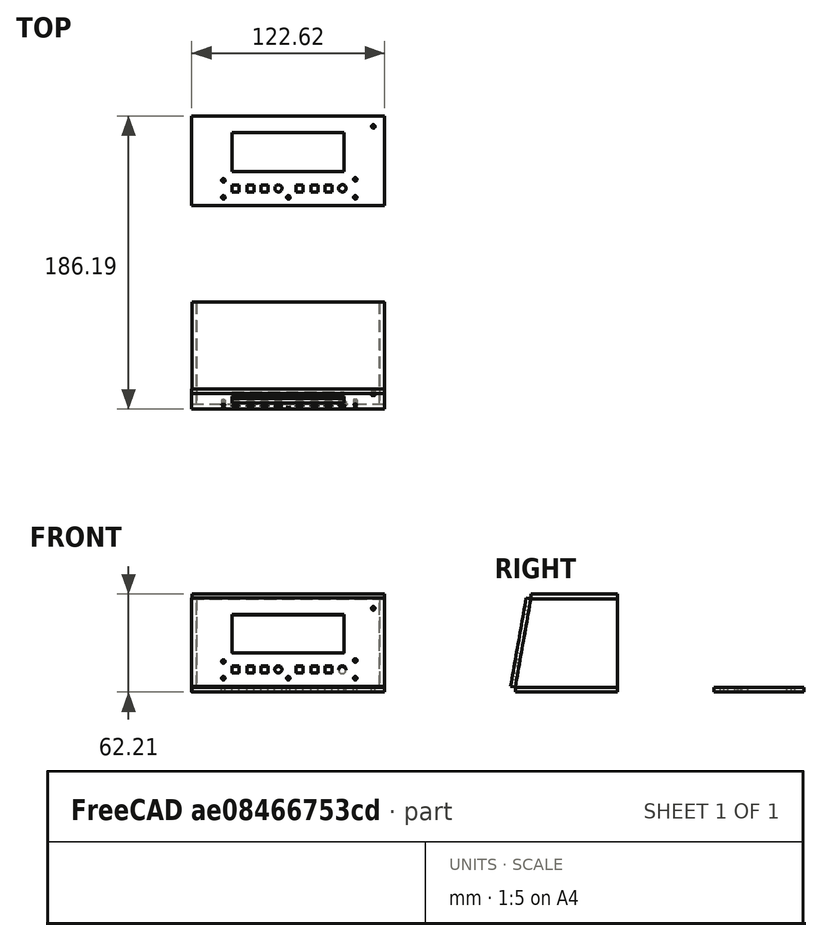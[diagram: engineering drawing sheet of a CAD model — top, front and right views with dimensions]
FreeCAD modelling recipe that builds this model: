
FCSTD DOCUMENT  (FreeCAD 0.14R2935 (Git))
Label: smart-timer-case
License: CC-BY 3.0
LicenseURL: http://creativecommons.org/licenses/by/3.0/
objects: Part::Feature×21, Part::Extrusion×20, Part::Cut×13
note: 54 computed .brp shape members not serialized (recipe doc carries the construction recipe); baked Part::Feature solids carry a one-line shape summary decoded from their .brp

FEATURE [Part::Feature] path7047
  shape: bbox 2.212 x 2.212 x 2e-07 mm, 1 faces, 0 solids (baked)
FEATURE [Part::Feature] path7051
  shape: bbox 2.212 x 2.212 x 2e-07 mm, 1 faces, 0 solids (baked)
FEATURE [Part::Feature] path7055
  shape: bbox 2.212 x 2.212 x 2e-07 mm, 1 faces, 0 solids (baked)
FEATURE [Part::Feature] path7063
  shape: bbox 2.212 x 2.212 x 2e-07 mm, 1 faces, 0 solids (baked)
FEATURE [Part::Feature] path7067
  shape: bbox 2.212 x 2.212 x 2e-07 mm, 1 faces, 0 solids (baked)
FEATURE [Part::Feature] path7075
  shape: bbox 2.212 x 2.212 x 2e-07 mm, 1 faces, 0 solids (baked)
FEATURE [Part::Feature] rect8425
  shape: bbox 4.462 x 4.462 x 2e-07 mm, 1 faces, 0 solids (baked)
FEATURE [Part::Feature] rect8425_9
  shape: bbox 4.462 x 4.462 x 2e-07 mm, 1 faces, 0 solids (baked)
FEATURE [Part::Feature] rect8425_4
  shape: bbox 4.462 x 4.462 x 2e-07 mm, 1 faces, 0 solids (baked)
FEATURE [Part::Feature] path8608
  shape: bbox 4.914 x 4.914 x 2e-07 mm, 1 faces, 0 solids (baked)
FEATURE [Part::Feature] rect8425_3
  shape: bbox 4.462 x 4.462 x 2e-07 mm, 1 faces, 0 solids (baked)
FEATURE [Part::Feature] rect8425_5
  shape: bbox 4.462 x 4.462 x 2e-07 mm, 1 faces, 0 solids (baked)
FEATURE [Part::Feature] rect8425_49
  shape: bbox 4.462 x 4.462 x 2e-07 mm, 1 faces, 0 solids (baked)
FEATURE [Part::Feature] path8608_5
  Placement = pos=(281.052,-140.182,0) rot=(0,0,1;0rad)
  shape: bbox 4.914 x 4.914 x 2e-07 mm, 1 faces, 0 solids (baked)
FEATURE [Part::Feature] rect8662
  shape: bbox 71.18 x 24.88 x 2e-07 mm, 1 faces, 0 solids (baked)
FEATURE [Part::Feature] rect9340
  shape: bbox 122.4 x 56.95 x 2e-07 mm, 1 faces, 0 solids (baked)
FEATURE [Part::Feature] rect5003
  shape: bbox 64.91 x 56.21 x 2e-07 mm, 1 faces, 0 solids (baked)
FEATURE [Part::Feature] rect5003_4
  shape: bbox 64.91 x 56.21 x 2e-07 mm, 1 faces, 0 solids (baked)
FEATURE [Part::Feature] rect5066
  shape: bbox 122.3 x 64.89 x 2e-07 mm, 1 faces, 0 solids (baked)
FEATURE [Part::Feature] rect5072
  shape: bbox 55.05 x 122.3 x 2e-07 mm, 1 faces, 0 solids (baked)
FEATURE [Part::Extrusion] Extrude
  Base = -> path7047
  Dir = (0,0,3)
  Solid = false
FEATURE [Part::Extrusion] Extrude001
  Base = -> path7051
  Dir = (0,0,3)
  Solid = false
FEATURE [Part::Extrusion] Extrude002
  Base = -> path7055
  Dir = (0,0,3)
  Solid = false
FEATURE [Part::Extrusion] Extrude003
  Base = -> path7063
  Dir = (0,0,3)
  Solid = false
FEATURE [Part::Extrusion] Extrude004
  Base = -> path7067
  Dir = (0,0,3)
  Solid = false
FEATURE [Part::Extrusion] Extrude005
  Base = -> path7075
  Dir = (0,0,3)
  Solid = false
FEATURE [Part::Extrusion] Extrude006
  Base = -> rect8425
  Dir = (0,0,3)
  Solid = false
FEATURE [Part::Extrusion] Extrude007
  Base = -> rect8425_9
  Dir = (0,0,3)
  Solid = false
FEATURE [Part::Extrusion] Extrude008
  Base = -> rect8425_4
  Dir = (0,0,3)
  Solid = false
FEATURE [Part::Extrusion] Extrude009
  Base = -> path8608
  Dir = (0,0,3)
  Solid = false
FEATURE [Part::Extrusion] Extrude010
  Base = -> rect8425_3
  Dir = (0,0,3)
  Solid = false
FEATURE [Part::Extrusion] Extrude011
  Base = -> rect8425_5
  Dir = (0,0,3)
  Solid = false
FEATURE [Part::Extrusion] Extrude012
  Base = -> rect8425_49
  Dir = (0,0,3)
  Solid = false
FEATURE [Part::Extrusion] Extrude013
  Base = -> path8608_5
  Dir = (0,0,3)
  Solid = false
FEATURE [Part::Extrusion] Extrude014
  Base = -> rect8662
  Dir = (0,0,3)
  Solid = false
FEATURE [Part::Extrusion] Extrude015
  Base = -> rect9340
  Dir = (0,0,3)
  Solid = false
FEATURE [Part::Extrusion] Extrude016
  Base = -> rect5003
  Dir = (0,0,3)
  Placement = pos=(6.62061,-118.12,121.816) rot=(0.57735,-0.57735,-0.57735;2.0944rad)
  Solid = false
FEATURE [Part::Extrusion] Extrude017
  Base = -> rect5003_4
  Dir = (0,0,3)
  Placement = pos=(125.886,-249.152,-59.7744) rot=(-0.57735,-0.57735,0.57735;2.0944rad)
  Solid = false
FEATURE [Part::Extrusion] Extrude018
  Base = -> rect5066
  Dir = (0,0,3)
  Solid = false
FEATURE [Part::Extrusion] Extrude019
  Base = -> rect5072
  Dir = (0,0,3)
  Placement = pos=(-48.8804,-308.862,59.21) rot=(0,0,1;1.5708rad)
  Solid = false
FEATURE [Part::Cut] Cut
  Base = -> Extrude015
  Tool = -> Extrude014
FEATURE [Part::Cut] Cut001
  Base = -> Cut
  Tool = -> Extrude013
FEATURE [Part::Cut] Cut002
  Base = -> Cut001
  Tool = -> Extrude012
FEATURE [Part::Cut] Cut003
  Base = -> Cut002
  Tool = -> Extrude011
FEATURE [Part::Cut] Cut004
  Base = -> Cut003
  Tool = -> Extrude010
FEATURE [Part::Cut] Cut005
  Base = -> Cut004
  Tool = -> Extrude009
FEATURE [Part::Cut] Cut006
  Base = -> Cut005
  Tool = -> Extrude008
FEATURE [Part::Cut] Cut007
  Base = -> Cut006
  Tool = -> Extrude007
FEATURE [Part::Cut] Cut008
  Base = -> Cut007
  Tool = -> Extrude006
FEATURE [Part::Cut] Cut009
  Base = -> Cut008
  Tool = -> Extrude005
FEATURE [Part::Cut] Cut010
  Base = -> Cut009
  Tool = -> Extrude004
FEATURE [Part::Cut] Cut011
  Base = -> Cut010
  Tool = -> Extrude003
FEATURE [Part::Cut] Cut012
  Base = -> Cut011
  Tool = -> Extrude002
FEATURE [Part::Feature] Cut014_solid  label="Cut014 (Solid)"
  Placement = pos=(-0.0409854,-176.253,62.606) rot=(1,0,0;1.39725rad)
  shape: bbox 122.4 x 12.79 x 56.61 mm, 60 faces (baked)
